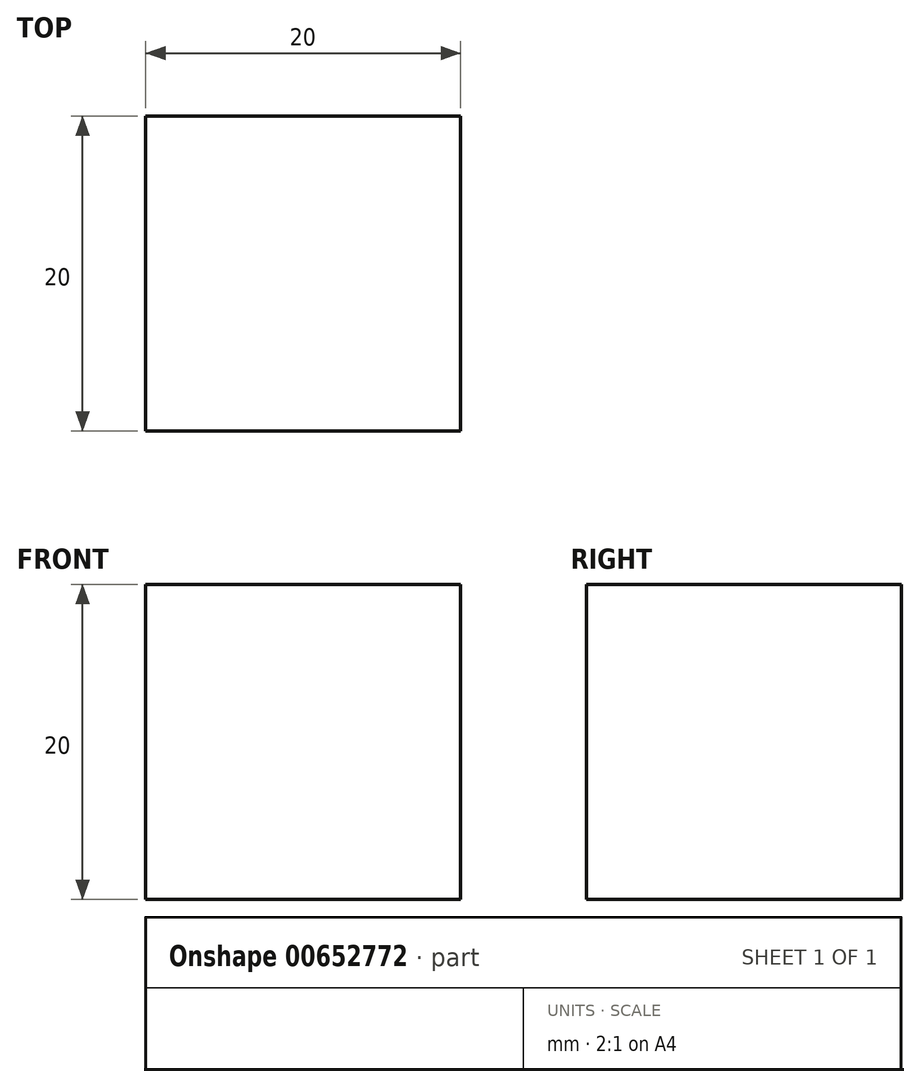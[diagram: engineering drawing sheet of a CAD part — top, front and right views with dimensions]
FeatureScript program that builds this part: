
annotation { "Feature Type Name" : "Feature", "Feature Type Description" : "" }
export const myFeature = defineFeature(function(context is Context, id is Id, definition is map)
    precondition{}
    {
        {
            var Q0;
            Q0=qCreatedBy(makeId("Top.planeOp"),FACE);
            var sketch = newSketch(context, id + "F0", { "sketchPlane" : qUnion([Q0])});
            skLineSegment(sketch, "E0.bottom", {"start": v(6.16, 5.6) * mm, "end": v(26.16, 5.6) * mm});
            skLineSegment(sketch, "E0.top", {"start": v(6.16, -14.4) * mm, "end": v(26.16, -14.4) * mm});
            skLineSegment(sketch, "E0.left", {"start": v(6.16, 5.6) * mm, "end": v(6.16, -14.4) * mm});
            skLineSegment(sketch, "E0.right", {"start": v(26.16, 5.6) * mm, "end": v(26.16, -14.4) * mm});
            skSolve(sketch);
        }
        {
            var Q0;
            Q0 = qSketchRegion(id + "F0", true);
            extrude(context, id + "F1", {"entities" : qUnion([Q0]), "depth" : 20 * mm, "offsetDistance" : 25 * mm});
        }
    });
